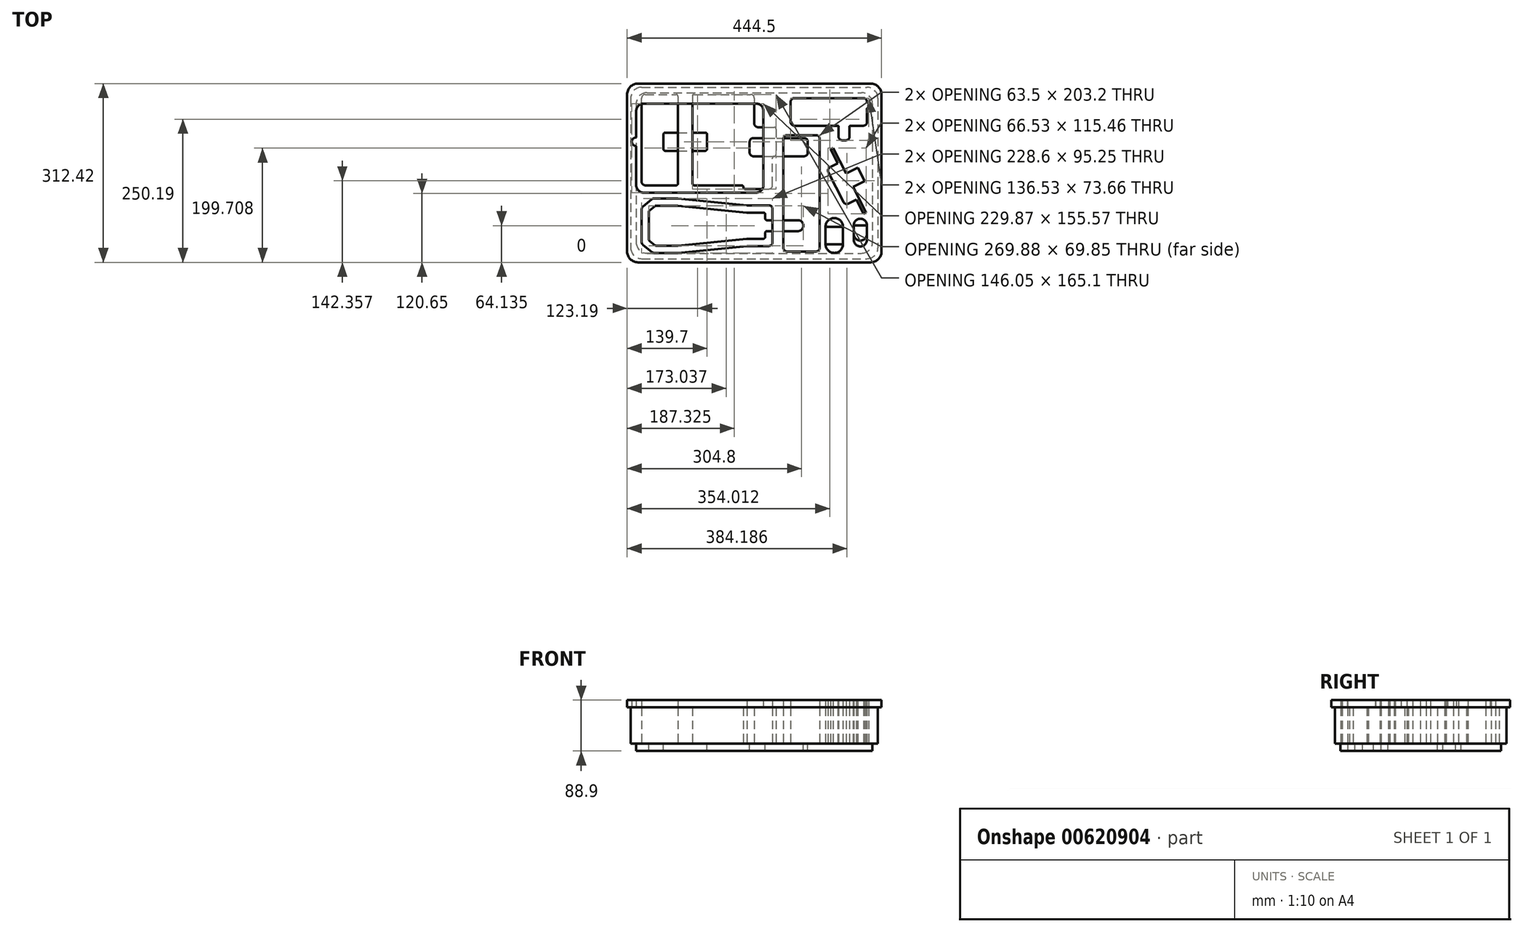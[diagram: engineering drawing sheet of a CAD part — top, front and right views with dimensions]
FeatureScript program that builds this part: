
annotation { "Feature Type Name" : "Feature", "Feature Type Description" : "" }
export const myFeature = defineFeature(function(context is Context, id is Id, definition is map)
    precondition{}
    {
        {
            var Q0;
            Q0=qCreatedBy(makeId("Top.planeOp"),FACE);
            var sketch = newSketch(context, id + "F0", { "sketchPlane" : qUnion([Q0])});
            skLineSegment(sketch, "E0.bottom", {"start": v(-196.85, 149.86) * mm, "end": v(196.85, 149.86) * mm});
            skLineSegment(sketch, "E0.top", {"start": v(-196.85, -149.86) * mm, "end": v(196.85, -149.86) * mm});
            skLineSegment(sketch, "E0.left", {"start": v(-215.9, 130.81) * mm, "end": v(-215.9, -130.81) * mm});
            skLineSegment(sketch, "E0.right", {"start": v(215.9, 130.81) * mm, "end": v(215.9, -130.8) * mm});
            skLineSegment(sketch, "E1.bottom", {"start": v(-196.85, -15.24) * mm, "end": v(-196.85, 130.81) * mm});
            skLineSegment(sketch, "E1.top", {"start": v(31.75, -21.59) * mm, "end": v(31.75, 26.04) * mm});
            skLineSegment(sketch, "E1.right", {"start": v(-190.5, 137.16) * mm, "end": v(-136.52, 137.16) * mm});
            skLineSegment(sketch, "E2.bottom", {"start": v(124.46, -93.98) * mm, "end": v(154.94, -93.98) * mm});
            skLineSegment(sketch, "E2.top", {"start": v(124.46, -124.46) * mm, "end": v(154.94, -124.46) * mm});
            skLineSegment(sketch, "E2.left", {"start": v(124.46, -93.98) * mm, "end": v(124.46, -124.46) * mm});
            skLineSegment(sketch, "E2.right", {"start": v(154.94, -93.98) * mm, "end": v(154.94, -124.46) * mm});
            skLineSegment(sketch, "E3", {"start": v(142.6, -24.8) * mm, "end": v(186.74, -2.32) * mm, "construction": true});
            skLineSegment(sketch, "E4", {"start": v(142.6, -24.8) * mm, "end": v(155.87, -50.83) * mm});
            skLineSegment(sketch, "E5", {"start": v(164.4, -53.6) * mm, "end": v(177.99, -46.7) * mm});
            skLineSegment(sketch, "E6", {"start": v(177.99, -46.7) * mm, "end": v(190.67, -71.59) * mm});
            skLineSegment(sketch, "E7", {"start": v(190.67, -71.59) * mm, "end": v(195.2, -69.28) * mm});
            skLineSegment(sketch, "E8", {"start": v(160.32, -0.82) * mm, "end": v(180.68, 9.56) * mm});
            skLineSegment(sketch, "E9", {"start": v(180.68, 9.56) * mm, "end": v(186.74, -2.32) * mm});
            skPoint(sketch, "E10.visualSharp", {"position": v(158.75, -56.5) * mm});
            skArc(sketch, "E10.filletArc", {"start": v(155.87, -50.83) * mm, "mid": v(159.56, -54) * mm, "end": v(164.4, -53.6) * mm});
            skArc(sketch, "E11.MirrorCS", {"start": v(129.35, 1.22) * mm, "mid": v(128.96, 6.06) * mm, "end": v(132.12, 9.76) * mm});
            skLineSegment(sketch, "E12.MirrorCS", {"start": v(145.7, 16.68) * mm, "end": v(133.02, 41.57) * mm});
            skLineSegment(sketch, "E13.MirrorCS", {"start": v(132.12, 9.76) * mm, "end": v(145.7, 16.68) * mm});
            skPoint(sketch, "E14.MirrorP", {"position": v(126.46, 6.88) * mm});
            skLineSegment(sketch, "E15.MirrorCS", {"start": v(172.42, -24.58) * mm, "end": v(192.8, -14.2) * mm});
            skLineSegment(sketch, "E16.MirrorCS", {"start": v(142.6, -24.8) * mm, "end": v(129.35, 1.22) * mm});
            skLineSegment(sketch, "E17.MirrorCS", {"start": v(192.8, -14.2) * mm, "end": v(186.74, -2.32) * mm});
            skLineSegment(sketch, "E18", {"start": v(172.42, -24.58) * mm, "end": v(195.2, -69.28) * mm});
            skPoint(sketch, "E19.visualSharp", {"position": v(-215.9, 149.86) * mm});
            skArc(sketch, "E19.filletArc", {"start": v(-196.85, 149.86) * mm, "mid": v(-210.32, 144.28) * mm, "end": v(-215.9, 130.81) * mm});
            skPoint(sketch, "E20.visualSharp", {"position": v(215.9, 149.86) * mm});
            skArc(sketch, "E20.filletArc", {"start": v(215.9, 130.81) * mm, "mid": v(210.32, 144.28) * mm, "end": v(196.85, 149.86) * mm});
            skPoint(sketch, "E21.visualSharp", {"position": v(215.9, -149.86) * mm});
            skArc(sketch, "E21.filletArc", {"start": v(196.85, -149.86) * mm, "mid": v(210.32, -144.28) * mm, "end": v(215.9, -130.8) * mm});
            skPoint(sketch, "E22.visualSharp", {"position": v(-215.9, -149.86) * mm});
            skArc(sketch, "E22.filletArc", {"start": v(-215.9, -130.81) * mm, "mid": v(-210.32, -144.28) * mm, "end": v(-196.85, -149.86) * mm});
            skPoint(sketch, "E23.visualSharp", {"position": v(-196.85, -27.94) * mm});
            skPoint(sketch, "E24.visualSharp", {"position": v(31.75, -27.94) * mm});
            skArc(sketch, "E24.filletArc", {"start": v(25.4, -27.94) * mm, "mid": v(29.9, -26.08) * mm, "end": v(31.75, -21.59) * mm});
            skPoint(sketch, "E25.visualSharp", {"position": v(-196.85, 137.16) * mm});
            skArc(sketch, "E25.filletArc", {"start": v(-190.5, 137.16) * mm, "mid": v(-195, 135.3) * mm, "end": v(-196.85, 130.81) * mm});
            skPoint(sketch, "E26.visualSharp", {"position": v(31.75, 137.16) * mm});
            skArc(sketch, "E26.filletArc", {"start": v(31.75, 130.81) * mm, "mid": v(29.9, 135.3) * mm, "end": v(25.4, 137.16) * mm, "construction": true});
            skLineSegment(sketch, "E27.bottom", {"start": v(63.5, 88.9) * mm, "end": v(63.5, 124.46) * mm});
            skLineSegment(sketch, "E27.top", {"start": v(196.85, 88.9) * mm, "end": v(196.85, 112.08) * mm});
            skLineSegment(sketch, "E27.left", {"start": v(69.85, 82.55) * mm, "end": v(146.05, 82.55) * mm});
            skLineSegment(sketch, "E27.right", {"start": v(69.85, 130.81) * mm, "end": v(190.5, 130.81) * mm});
            skLineSegment(sketch, "E28.bottom", {"start": v(147.32, 81.28) * mm, "end": v(147.32, 63.5) * mm});
            skLineSegment(sketch, "E28.top", {"start": v(166.37, 81.28) * mm, "end": v(166.37, 63.5) * mm});
            skLineSegment(sketch, "E28.right", {"start": v(153.67, 57.15) * mm, "end": v(160.02, 57.15) * mm});
            skLineSegment(sketch, "E29.trimOffspring", {"start": v(167.64, 82.55) * mm, "end": v(190.5, 82.55) * mm});
            skLineSegment(sketch, "E30", {"start": v(147.32, 82.55) * mm, "end": v(166.37, 82.55) * mm, "construction": true});
            skPoint(sketch, "E31.visualSharp", {"position": v(63.5, 82.55) * mm});
            skArc(sketch, "E31.filletArc", {"start": v(63.5, 88.9) * mm, "mid": v(65.36, 84.4) * mm, "end": v(69.85, 82.55) * mm});
            skPoint(sketch, "E32.visualSharp", {"position": v(196.85, 82.55) * mm});
            skArc(sketch, "E32.filletArc", {"start": v(190.5, 82.55) * mm, "mid": v(195, 84.4) * mm, "end": v(196.85, 88.9) * mm});
            skArc(sketch, "E33.filletArc", {"start": v(196.85, 124.46) * mm, "mid": v(195, 128.95) * mm, "end": v(190.5, 130.81) * mm});
            skPoint(sketch, "E34.visualSharp", {"position": v(63.5, 130.81) * mm});
            skArc(sketch, "E34.filletArc", {"start": v(69.85, 130.81) * mm, "mid": v(65.36, 128.95) * mm, "end": v(63.5, 124.46) * mm});
            skPoint(sketch, "E35.visualSharp", {"position": v(147.32, 57.15) * mm});
            skArc(sketch, "E35.filletArc", {"start": v(147.32, 63.5) * mm, "mid": v(149.18, 59) * mm, "end": v(153.67, 57.15) * mm});
            skPoint(sketch, "E36.visualSharp", {"position": v(166.37, 57.15) * mm});
            skArc(sketch, "E36.filletArc", {"start": v(160.02, 57.15) * mm, "mid": v(164.51, 59) * mm, "end": v(166.37, 63.5) * mm});
            skLineSegment(sketch, "E37.bottom", {"start": v(173.74, -91.44) * mm, "end": v(196.85, -91.44) * mm});
            skLineSegment(sketch, "E37.left", {"start": v(173.74, -91.44) * mm, "end": v(173.74, -106.68) * mm});
            skLineSegment(sketch, "E37.right", {"start": v(196.85, -91.44) * mm, "end": v(196.85, -106.68) * mm});
            skArc(sketch, "E38", {"start": v(173.74, -106.68) * mm, "mid": v(185.3, -118.24) * mm, "end": v(196.85, -106.68) * mm});
            skLineSegment(sketch, "E39.bottom", {"start": v(-196.85, -139.7) * mm, "end": v(-196.85, -44.45) * mm, "construction": true});
            skLineSegment(sketch, "E39.top", {"start": v(31.75, -139.7) * mm, "end": v(31.75, -44.45) * mm, "construction": true});
            skLineSegment(sketch, "E39.left", {"start": v(-196.85, -139.7) * mm, "end": v(31.75, -139.7) * mm, "construction": true});
            skLineSegment(sketch, "E39.right", {"start": v(-196.85, -44.45) * mm, "end": v(31.75, -44.45) * mm, "construction": true});
            skLineSegment(sketch, "E40", {"start": v(-196.85, -92.08) * mm, "end": v(31.75, -92.07) * mm, "construction": true});
            skLineSegment(sketch, "E41", {"start": v(-196.85, -123.83) * mm, "end": v(31.75, -123.82) * mm, "construction": true});
            skLineSegment(sketch, "E42.MirrorCS", {"start": v(-196.85, -60.33) * mm, "end": v(31.75, -60.32) * mm, "construction": true});
            skLineSegment(sketch, "E43", {"start": v(-196.85, -127.64) * mm, "end": v(31.75, -127.63) * mm, "construction": true});
            skLineSegment(sketch, "E44.MirrorCS", {"start": v(-196.85, -56.51) * mm, "end": v(31.75, -56.51) * mm, "construction": true});
            skLineSegment(sketch, "E45", {"start": v(-177.16, -139.7) * mm, "end": v(-177.16, -44.45) * mm, "construction": true});
            skLineSegment(sketch, "E46", {"start": v(-133.35, -139.7) * mm, "end": v(-133.35, -44.45) * mm, "construction": true});
            skLineSegment(sketch, "E47", {"start": v(-12.7, -139.7) * mm, "end": v(-12.7, -44.45) * mm, "construction": true});
            skLineSegment(sketch, "E48", {"start": v(-196.85, -120.79) * mm, "end": v(-196.85, -63.36) * mm});
            skLineSegment(sketch, "E49", {"start": v(-194.49, -58.42) * mm, "end": v(-178.9, -45.86) * mm});
            skLineSegment(sketch, "E50", {"start": v(-174.92, -44.45) * mm, "end": v(-133.35, -44.45) * mm});
            skLineSegment(sketch, "E51", {"start": v(-133.35, -44.45) * mm, "end": v(-12.7, -56.51) * mm});
            skLineSegment(sketch, "E52", {"start": v(-12.7, -56.51) * mm, "end": v(25.4, -56.51) * mm});
            skLineSegment(sketch, "E53", {"start": v(31.75, -62.86) * mm, "end": v(31.75, -121.28) * mm});
            skLineSegment(sketch, "E54", {"start": v(25.4, -127.63) * mm, "end": v(-12.7, -127.63) * mm});
            skLineSegment(sketch, "E55", {"start": v(-12.7, -127.64) * mm, "end": v(-133.35, -139.7) * mm});
            skLineSegment(sketch, "E56", {"start": v(-133.35, -139.7) * mm, "end": v(-174.92, -139.7) * mm});
            skLineSegment(sketch, "E57", {"start": v(-178.9, -138.3) * mm, "end": v(-194.49, -125.73) * mm});
            skPoint(sketch, "E58.visualSharp", {"position": v(31.75, -127.64) * mm});
            skArc(sketch, "E58.filletArc", {"start": v(25.4, -127.63) * mm, "mid": v(29.9, -125.78) * mm, "end": v(31.75, -121.28) * mm});
            skPoint(sketch, "E59.visualSharp", {"position": v(31.75, -56.51) * mm});
            skArc(sketch, "E59.filletArc", {"start": v(31.75, -62.86) * mm, "mid": v(29.9, -58.37) * mm, "end": v(25.4, -56.51) * mm});
            skPoint(sketch, "E60.visualSharp", {"position": v(-196.85, -123.83) * mm});
            skArc(sketch, "E60.filletArc", {"start": v(-196.85, -120.79) * mm, "mid": v(-196.23, -123.53) * mm, "end": v(-194.49, -125.73) * mm});
            skPoint(sketch, "E61.visualSharp", {"position": v(-177.16, -139.7) * mm});
            skArc(sketch, "E61.filletArc", {"start": v(-178.9, -138.3) * mm, "mid": v(-177.04, -139.34) * mm, "end": v(-174.92, -139.7) * mm});
            skPoint(sketch, "E62.visualSharp", {"position": v(-196.85, -60.33) * mm});
            skArc(sketch, "E62.filletArc", {"start": v(-194.49, -58.42) * mm, "mid": v(-196.23, -60.62) * mm, "end": v(-196.85, -63.36) * mm});
            skPoint(sketch, "E63.visualSharp", {"position": v(-177.16, -44.45) * mm});
            skArc(sketch, "E63.filletArc", {"start": v(-174.92, -44.45) * mm, "mid": v(-177.04, -44.81) * mm, "end": v(-178.9, -45.86) * mm});
            skLineSegment(sketch, "E64", {"start": v(173.74, -106.68) * mm, "end": v(196.85, -106.68) * mm, "construction": true});
            skLineSegment(sketch, "E65.MirrorCS", {"start": v(160.32, -0.82) * mm, "end": v(137.54, 43.88) * mm});
            skLineSegment(sketch, "E66.MirrorCS", {"start": v(133.02, 41.57) * mm, "end": v(137.54, 43.88) * mm});
            skLineSegment(sketch, "E67", {"start": v(198.12, 122.87) * mm, "end": v(198.76, 122.87) * mm});
            skLineSegment(sketch, "E68", {"start": v(200.02, 121.6) * mm, "end": v(200.02, 114.62) * mm});
            skLineSegment(sketch, "E69", {"start": v(198.76, 113.35) * mm, "end": v(198.12, 113.35) * mm});
            skPoint(sketch, "E70.visualSharp", {"position": v(166.37, 82.55) * mm});
            skArc(sketch, "E70.filletArc", {"start": v(167.64, 82.55) * mm, "mid": v(166.74, 82.18) * mm, "end": v(166.37, 81.28) * mm});
            skPoint(sketch, "E71.visualSharp", {"position": v(147.32, 82.55) * mm});
            skArc(sketch, "E71.filletArc", {"start": v(147.32, 81.28) * mm, "mid": v(146.95, 82.18) * mm, "end": v(146.05, 82.55) * mm});
            skPoint(sketch, "E72.visualSharp", {"position": v(200.03, 113.35) * mm});
            skArc(sketch, "E72.filletArc", {"start": v(198.76, 113.35) * mm, "mid": v(199.65, 113.72) * mm, "end": v(200.03, 114.62) * mm});
            skPoint(sketch, "E73.visualSharp", {"position": v(200.03, 122.87) * mm});
            skArc(sketch, "E73.filletArc", {"start": v(200.02, 121.6) * mm, "mid": v(199.65, 122.5) * mm, "end": v(198.76, 122.87) * mm});
            skPoint(sketch, "E74.visualSharp", {"position": v(196.85, 122.87) * mm});
            skArc(sketch, "E74.filletArc", {"start": v(196.85, 124.13) * mm, "mid": v(197.23, 123.24) * mm, "end": v(198.12, 122.87) * mm});
            skPoint(sketch, "E75.visualSharp", {"position": v(196.85, 113.35) * mm});
            skArc(sketch, "E75.filletArc", {"start": v(198.12, 113.35) * mm, "mid": v(197.22, 112.98) * mm, "end": v(196.85, 112.08) * mm});
            skLineSegment(sketch, "E76", {"start": v(-196.85, 54.61) * mm, "end": v(31.75, 54.61) * mm, "construction": true});
            skLineSegment(sketch, "E77", {"start": v(-82.55, -27.94) * mm, "end": v(-82.55, 137.16) * mm, "construction": true});
            skLineSegment(sketch, "E78", {"start": v(0, 149.86) * mm, "end": v(0, -149.86) * mm, "construction": true});
            skLineSegment(sketch, "E79", {"start": v(-215.9, 0) * mm, "end": v(215.9, 0) * mm, "construction": true});
            skPoint(sketch, "E80", {"position": v(0, 0) * mm});
            skPoint(sketch, "E81", {"position": v(-82.55, 54.61) * mm});
            skPoint(sketch, "E82", {"position": v(-133.35, -92.08) * mm});
            skLineSegment(sketch, "E83", {"start": v(63.5, 106.68) * mm, "end": v(196.85, 106.68) * mm, "construction": true});
            skLineSegment(sketch, "E84", {"start": v(130.18, 130.81) * mm, "end": v(130.18, 82.55) * mm, "construction": true});
            skPoint(sketch, "E85", {"position": v(130.18, 106.68) * mm});
            skLineSegment(sketch, "E86", {"start": v(172.42, -24.58) * mm, "end": v(160.32, -0.82) * mm, "construction": true});
            skPoint(sketch, "E87", {"position": v(166.37, -12.7) * mm});
            skLineSegment(sketch, "E88", {"start": v(196.85, 124.46) * mm, "end": v(196.85, 124.13) * mm});
            skLineSegment(sketch, "E89", {"start": v(196.85, 124.13) * mm, "end": v(196.85, 112.08) * mm, "construction": true});
            skArc(sketch, "E90", {"start": v(31.75, -21.59) * mm, "mid": v(29.9, -26.08) * mm, "end": v(25.4, -27.94) * mm});
            skLineSegment(sketch, "E91.bottom", {"start": v(107.95, -137.16) * mm, "end": v(57.15, -137.16) * mm});
            skLineSegment(sketch, "E91.top", {"start": v(107.95, 66.04) * mm, "end": v(57.15, 66.04) * mm});
            skLineSegment(sketch, "E91.left", {"start": v(114.3, -130.8) * mm, "end": v(114.3, 59.7) * mm});
            skLineSegment(sketch, "E91.right", {"start": v(50.8, -130.8) * mm, "end": v(50.8, 59.7) * mm});
            skLineSegment(sketch, "E92", {"start": v(82.55, -137.16) * mm, "end": v(82.55, 66.04) * mm, "construction": true});
            skLineSegment(sketch, "E93", {"start": v(114.3, -35.56) * mm, "end": v(50.8, -35.56) * mm, "construction": true});
            skPoint(sketch, "E94", {"position": v(82.55, -35.56) * mm});
            skPoint(sketch, "E95.visualSharp", {"position": v(114.3, -137.16) * mm});
            skArc(sketch, "E95.filletArc", {"start": v(107.95, -137.16) * mm, "mid": v(112.44, -135.3) * mm, "end": v(114.3, -130.8) * mm});
            skPoint(sketch, "E96.visualSharp", {"position": v(50.8, -137.16) * mm});
            skArc(sketch, "E96.filletArc", {"start": v(50.8, -130.8) * mm, "mid": v(52.66, -135.3) * mm, "end": v(57.15, -137.16) * mm});
            skPoint(sketch, "E97.visualSharp", {"position": v(50.8, 66.04) * mm});
            skArc(sketch, "E97.filletArc", {"start": v(57.15, 66.04) * mm, "mid": v(52.66, 64.18) * mm, "end": v(50.8, 59.7) * mm});
            skPoint(sketch, "E98.visualSharp", {"position": v(114.3, 66.04) * mm});
            skArc(sketch, "E98.filletArc", {"start": v(114.3, 59.7) * mm, "mid": v(112.44, 64.18) * mm, "end": v(107.95, 66.04) * mm});
            skLineSegment(sketch, "E99.left", {"start": v(-107.95, 133.99) * mm, "end": v(-107.95, -18.41) * mm});
            skLineSegment(sketch, "E99.right", {"start": v(-133.35, 133.99) * mm, "end": v(-133.35, -18.41) * mm});
            skLineSegment(sketch, "E100", {"start": v(34.93, 80.01) * mm, "end": v(34.92, 80.01) * mm});
            skLineSegment(sketch, "E101.MirrorCS", {"start": v(34.93, 29.21) * mm, "end": v(34.93, 29.21) * mm});
            skLineSegment(sketch, "E102", {"start": v(38.1, 76.84) * mm, "end": v(38.1, 32.39) * mm});
            skLineSegment(sketch, "E103", {"start": v(-104.77, 137.16) * mm, "end": v(-6.35, 137.16) * mm});
            skLineSegment(sketch, "E104", {"start": v(31.75, 83.19) * mm, "end": v(31.75, 130.81) * mm, "construction": true});
            skLineSegment(sketch, "E105", {"start": v(31.75, 29.21) * mm, "end": v(31.75, 80.01) * mm, "construction": true});
            skLineSegment(sketch, "E106", {"start": v(-133.35, 137.16) * mm, "end": v(-107.95, 137.16) * mm, "construction": true});
            skPoint(sketch, "E107.visualSharp", {"position": v(-107.95, 137.16) * mm});
            skArc(sketch, "E107.filletArc", {"start": v(-104.77, 137.16) * mm, "mid": v(-107.02, 136.23) * mm, "end": v(-107.95, 133.99) * mm});
            skPoint(sketch, "E108.visualSharp", {"position": v(-133.35, 137.16) * mm});
            skArc(sketch, "E108.filletArc", {"start": v(-133.35, 133.99) * mm, "mid": v(-134.28, 136.23) * mm, "end": v(-136.52, 137.16) * mm});
            skPoint(sketch, "E109.visualSharp", {"position": v(31.75, 80.01) * mm});
            skPoint(sketch, "E110.visualSharp", {"position": v(31.75, 29.21) * mm});
            skArc(sketch, "E110.filletArc", {"start": v(34.93, 29.21) * mm, "mid": v(32.68, 28.28) * mm, "end": v(31.75, 26.04) * mm});
            skPoint(sketch, "E111.visualSharp", {"position": v(38.1, 29.21) * mm});
            skArc(sketch, "E111.filletArc", {"start": v(34.93, 29.21) * mm, "mid": v(37.17, 30.14) * mm, "end": v(38.1, 32.39) * mm});
            skPoint(sketch, "E112.visualSharp", {"position": v(38.1, 80.01) * mm});
            skArc(sketch, "E112.filletArc", {"start": v(38.1, 76.84) * mm, "mid": v(37.17, 79.08) * mm, "end": v(34.92, 80.01) * mm});
            skLineSegment(sketch, "E113", {"start": v(0, 130.81) * mm, "end": v(0, 86.36) * mm});
            skLineSegment(sketch, "E114", {"start": v(6.35, 80.01) * mm, "end": v(34.93, 80.01) * mm});
            skPoint(sketch, "E115.visualSharp", {"position": v(0, 80.01) * mm});
            skArc(sketch, "E115.filletArc", {"start": v(0, 86.36) * mm, "mid": v(1.86, 81.87) * mm, "end": v(6.35, 80.01) * mm});
            skLineSegment(sketch, "E116", {"start": v(-6.35, 137.16) * mm, "end": v(0, 137.16) * mm, "construction": true});
            skLineSegment(sketch, "E117", {"start": v(0, 137.16) * mm, "end": v(25.4, 137.16) * mm, "construction": true});
            skPoint(sketch, "E118.visualSharp", {"position": v(0, 137.16) * mm});
            skArc(sketch, "E118.filletArc", {"start": v(0, 130.81) * mm, "mid": v(-1.86, 135.3) * mm, "end": v(-6.35, 137.16) * mm});
            skLineSegment(sketch, "E119", {"start": v(-6.35, 137.16) * mm, "end": v(-6.35, 137.16) * mm});
            skLineSegment(sketch, "E120", {"start": v(-19.05, -24.76) * mm, "end": v(-19.05, -24.76) * mm});
            skLineSegment(sketch, "E121", {"start": v(-22.22, -21.59) * mm, "end": v(-104.78, -21.59) * mm});
            skLineSegment(sketch, "E122", {"start": v(-133.35, -21.59) * mm, "end": v(-133.35, -24.76) * mm, "construction": true});
            skLineSegment(sketch, "E123", {"start": v(-15.88, -27.94) * mm, "end": v(25.4, -27.94) * mm});
            skLineSegment(sketch, "E124", {"start": v(-107.95, -21.59) * mm, "end": v(-107.95, -24.76) * mm, "construction": true});
            skPoint(sketch, "E125.visualSharp", {"position": v(-196.85, -21.59) * mm});
            skArc(sketch, "E125.filletArc", {"start": v(-196.85, -15.24) * mm, "mid": v(-195, -19.73) * mm, "end": v(-190.5, -21.59) * mm});
            skPoint(sketch, "E126.visualSharp", {"position": v(-19.05, -21.59) * mm});
            skArc(sketch, "E126.filletArc", {"start": v(-19.05, -24.76) * mm, "mid": v(-19.98, -22.52) * mm, "end": v(-22.22, -21.59) * mm});
            skPoint(sketch, "E127.visualSharp", {"position": v(-19.05, -27.94) * mm});
            skArc(sketch, "E127.filletArc", {"start": v(-19.05, -24.76) * mm, "mid": v(-18.12, -27.01) * mm, "end": v(-15.88, -27.94) * mm});
            skLineSegment(sketch, "E128", {"start": v(-136.53, -21.59) * mm, "end": v(-190.5, -21.59) * mm});
            skPoint(sketch, "E129.visualSharp", {"position": v(-133.35, -21.59) * mm});
            skArc(sketch, "E129.filletArc", {"start": v(-136.53, -21.59) * mm, "mid": v(-134.28, -20.66) * mm, "end": v(-133.35, -18.41) * mm});
            skPoint(sketch, "E130.visualSharp", {"position": v(-107.95, -21.59) * mm});
            skArc(sketch, "E130.filletArc", {"start": v(-107.95, -18.41) * mm, "mid": v(-107.02, -20.66) * mm, "end": v(-104.78, -21.59) * mm});
            skSolve(sketch);
        }
        {
            var Q0;
            Q0=qSketchRegion(id+"F0",true);
            extrude(context, id + "F1", {"entities" : qUnion([Q0]), "depth" : 63.5 * mm, "offsetDistance" : 25.4 * mm});
        }
        {
            var Q0;
            Q0=qCreatedBy(makeId("Top.planeOp"),FACE);
            var sketch = newSketch(context, id + "F2", { "sketchPlane" : qUnion([Q0])});
            skLineSegment(sketch, "E131.0", {"start": v(-215.9, 149.86) * mm, "end": v(215.9, 149.86) * mm, "construction": true});
            skLineSegment(sketch, "E132.0", {"start": v(-215.9, 149.86) * mm, "end": v(-215.9, -149.86) * mm, "construction": true});
            skLineSegment(sketch, "E133.0", {"start": v(215.9, 149.86) * mm, "end": v(215.9, -149.86) * mm, "construction": true});
            skLineSegment(sketch, "E134.0", {"start": v(-190.26, -149.86) * mm, "end": v(215.9, -149.86) * mm, "construction": true});
            skPoint(sketch, "E135.orphan", {"position": v(-196.85, 149.86) * mm});
            skPoint(sketch, "E136.orphan", {"position": v(-215.9, 130.81) * mm});
            skPoint(sketch, "E137.orphan", {"position": v(196.85, 149.86) * mm});
            skPoint(sketch, "E138.orphan", {"position": v(215.9, 130.81) * mm});
            skPoint(sketch, "E139.orphan", {"position": v(215.9, -130.8) * mm});
            skPoint(sketch, "E140.orphan", {"position": v(196.85, -149.86) * mm});
            skPoint(sketch, "E141.orphan", {"position": v(-196.85, -149.86) * mm});
            skPoint(sketch, "E142.orphan", {"position": v(-215.9, -130.81) * mm});
            skPoint(sketch, "E143", {"position": v(0, 0) * mm});
            skLineSegment(sketch, "E144", {"start": v(0, 149.86) * mm, "end": v(0, -149.86) * mm, "construction": true});
            skPoint(sketch, "E144.startSnap0", {"position": v(0, 149.86) * mm});
            skLineSegment(sketch, "E145", {"start": v(-215.9, 0) * mm, "end": v(215.9, 0) * mm, "construction": true});
            skLineSegment(sketch, "E146.bottom", {"start": v(-187.32, 140.34) * mm, "end": v(187.33, 140.34) * mm});
            skLineSegment(sketch, "E146.top", {"start": v(-187.33, -140.33) * mm, "end": v(187.32, -140.33) * mm});
            skLineSegment(sketch, "E146.left", {"start": v(-206.38, 121.29) * mm, "end": v(-206.38, -121.28) * mm});
            skLineSegment(sketch, "E146.right", {"start": v(206.38, 121.29) * mm, "end": v(206.38, -121.28) * mm});
            skPoint(sketch, "E147.visualSharp", {"position": v(-206.38, 140.34) * mm});
            skPoint(sketch, "E148.visualSharp", {"position": v(206.38, 140.34) * mm});
            skPoint(sketch, "E149.visualSharp", {"position": v(206.38, -140.33) * mm});
            skPoint(sketch, "E150.visualSharp", {"position": v(-206.38, -140.33) * mm});
            skLineSegment(sketch, "E151.0.0", {"start": v(-12.7, -127.63) * mm, "end": v(25.4, -127.63) * mm, "construction": true});
            skArc(sketch, "E151.0.1", {"start": v(25.4, -127.63) * mm, "mid": v(29.9, -125.78) * mm, "end": v(31.75, -121.28) * mm, "construction": true});
            skLineSegment(sketch, "E151.0.2", {"start": v(31.75, -121.28) * mm, "end": v(31.75, -62.86) * mm, "construction": true});
            skArc(sketch, "E151.0.3", {"start": v(31.75, -62.86) * mm, "mid": v(29.9, -58.37) * mm, "end": v(25.4, -56.51) * mm, "construction": true});
            skLineSegment(sketch, "E151.0.4", {"start": v(25.4, -56.51) * mm, "end": v(-12.7, -56.51) * mm, "construction": true});
            skLineSegment(sketch, "E151.0.5", {"start": v(-12.7, -56.52) * mm, "end": v(-133.35, -44.45) * mm, "construction": true});
            skLineSegment(sketch, "E151.0.6", {"start": v(-133.35, -44.45) * mm, "end": v(-174.92, -44.45) * mm, "construction": true});
            skArc(sketch, "E151.0.7", {"start": v(-174.92, -44.45) * mm, "mid": v(-177.04, -44.81) * mm, "end": v(-178.9, -45.86) * mm, "construction": true});
            skLineSegment(sketch, "E151.0.8", {"start": v(-178.9, -45.86) * mm, "end": v(-194.49, -58.42) * mm, "construction": true});
            skArc(sketch, "E151.0.9", {"start": v(-194.49, -58.42) * mm, "mid": v(-196.23, -60.62) * mm, "end": v(-196.85, -63.36) * mm, "construction": true});
            skLineSegment(sketch, "E151.0.10", {"start": v(-196.85, -63.36) * mm, "end": v(-196.85, -120.79) * mm, "construction": true});
            skArc(sketch, "E151.0.11", {"start": v(-196.85, -120.79) * mm, "mid": v(-196.23, -123.53) * mm, "end": v(-194.49, -125.73) * mm, "construction": true});
            skLineSegment(sketch, "E151.0.12", {"start": v(-194.49, -125.73) * mm, "end": v(-178.9, -138.3) * mm, "construction": true});
            skArc(sketch, "E151.0.13", {"start": v(-178.9, -138.3) * mm, "mid": v(-177.04, -139.34) * mm, "end": v(-174.92, -139.7) * mm, "construction": true});
            skLineSegment(sketch, "E151.0.14", {"start": v(-174.92, -139.7) * mm, "end": v(-133.35, -139.7) * mm, "construction": true});
            skLineSegment(sketch, "E151.0.15", {"start": v(-133.35, -139.7) * mm, "end": v(-12.7, -127.64) * mm, "construction": true});
            skArc(sketch, "E152.filletArc", {"start": v(-187.32, 140.34) * mm, "mid": v(-200.8, 134.76) * mm, "end": v(-206.38, 121.29) * mm});
            skArc(sketch, "E153.filletArc", {"start": v(206.38, 121.29) * mm, "mid": v(200.8, 134.76) * mm, "end": v(187.33, 140.34) * mm});
            skArc(sketch, "E154.filletArc", {"start": v(187.32, -140.33) * mm, "mid": v(200.8, -134.76) * mm, "end": v(206.37, -121.28) * mm});
            skArc(sketch, "E155.filletArc", {"start": v(-206.38, -121.28) * mm, "mid": v(-200.8, -134.76) * mm, "end": v(-187.33, -140.33) * mm});
            skLineSegment(sketch, "E156.0", {"start": v(-173.55, -57.85) * mm, "end": v(-182.97, -65.45) * mm});
            skLineSegment(sketch, "E156.1", {"start": v(-134.14, -57.15) * mm, "end": v(-171.56, -57.15) * mm});
            skLineSegment(sketch, "E156.2", {"start": v(-184.15, -67.92) * mm, "end": v(-184.15, -116.23) * mm});
            skLineSegment(sketch, "E156.3", {"start": v(-13.5, -69.2) * mm, "end": v(-133.83, -57.17) * mm});
            skLineSegment(sketch, "E156.4", {"start": v(15.88, -69.21) * mm, "end": v(-13.18, -69.21) * mm});
            skLineSegment(sketch, "E156.5", {"start": v(19.05, -111.76) * mm, "end": v(19.05, -104.78) * mm});
            skLineSegment(sketch, "E156.6", {"start": v(-182.97, -118.7) * mm, "end": v(-173.55, -126.3) * mm});
            skLineSegment(sketch, "E156.7", {"start": v(-171.56, -127) * mm, "end": v(-134.14, -127) * mm});
            skLineSegment(sketch, "E156.8", {"start": v(-133.83, -126.98) * mm, "end": v(-13.5, -114.95) * mm});
            skLineSegment(sketch, "E156.9", {"start": v(-13.18, -114.93) * mm, "end": v(15.88, -114.93) * mm});
            skLineSegment(sketch, "E157", {"start": v(22.23, -82.55) * mm, "end": v(76.2, -82.55) * mm});
            skLineSegment(sketch, "E158", {"start": v(-184.15, -92.08) * mm, "end": v(76.2, -92.08) * mm, "construction": true});
            skLineSegment(sketch, "E159", {"start": v(76.2, -82.55) * mm, "end": v(76.2, -92.08) * mm, "construction": true});
            skLineSegment(sketch, "E160.MirrorCS", {"start": v(22.23, -101.6) * mm, "end": v(76.2, -101.6) * mm});
            skLineSegment(sketch, "E161.MirrorCS", {"start": v(76.2, -101.6) * mm, "end": v(76.2, -92.08) * mm, "construction": true});
            skLineSegment(sketch, "E162", {"start": v(19.05, -79.37) * mm, "end": v(19.05, -72.39) * mm});
            skPoint(sketch, "E163.orphan", {"position": v(19.05, -92.08) * mm});
            skArc(sketch, "E164", {"start": v(76.2, -82.55) * mm, "mid": v(85.73, -92.08) * mm, "end": v(76.2, -101.6) * mm});
            skLineSegment(sketch, "E165.bottom", {"start": v(-1.78, 60.96) * mm, "end": v(87.12, 60.96) * mm});
            skLineSegment(sketch, "E165.top", {"start": v(-1.78, 29.21) * mm, "end": v(87.12, 29.21) * mm});
            skLineSegment(sketch, "E165.left", {"start": v(-8.13, 54.61) * mm, "end": v(-8.13, 35.56) * mm});
            skLineSegment(sketch, "E165.right", {"start": v(93.47, 54.61) * mm, "end": v(93.47, 35.56) * mm});
            skPoint(sketch, "E166.visualSharp", {"position": v(-8.13, 60.96) * mm});
            skArc(sketch, "E166.filletArc", {"start": v(-1.78, 60.96) * mm, "mid": v(-6.27, 59.1) * mm, "end": v(-8.13, 54.61) * mm});
            skPoint(sketch, "E167.visualSharp", {"position": v(93.47, 60.96) * mm});
            skArc(sketch, "E167.filletArc", {"start": v(93.47, 54.61) * mm, "mid": v(91.61, 59.1) * mm, "end": v(87.12, 60.96) * mm});
            skPoint(sketch, "E168.visualSharp", {"position": v(93.47, 29.21) * mm});
            skArc(sketch, "E168.filletArc", {"start": v(87.12, 29.21) * mm, "mid": v(91.61, 31.07) * mm, "end": v(93.47, 35.56) * mm});
            skPoint(sketch, "E169.visualSharp", {"position": v(-8.13, 29.21) * mm});
            skArc(sketch, "E169.filletArc", {"start": v(-8.13, 35.56) * mm, "mid": v(-6.27, 31.07) * mm, "end": v(-1.78, 29.21) * mm});
            skPoint(sketch, "E170.visualSharp", {"position": v(19.05, -69.21) * mm});
            skArc(sketch, "E170.filletArc", {"start": v(19.05, -72.39) * mm, "mid": v(18.12, -70.14) * mm, "end": v(15.88, -69.21) * mm});
            skPoint(sketch, "E171.visualSharp", {"position": v(19.05, -82.55) * mm});
            skArc(sketch, "E171.filletArc", {"start": v(19.05, -79.37) * mm, "mid": v(19.98, -81.62) * mm, "end": v(22.23, -82.55) * mm});
            skPoint(sketch, "E172.visualSharp", {"position": v(19.05, -101.6) * mm});
            skArc(sketch, "E172.filletArc", {"start": v(22.23, -101.6) * mm, "mid": v(19.98, -102.53) * mm, "end": v(19.05, -104.78) * mm});
            skPoint(sketch, "E173.visualSharp", {"position": v(19.05, -114.94) * mm});
            skArc(sketch, "E173.filletArc", {"start": v(15.88, -114.94) * mm, "mid": v(18.12, -114) * mm, "end": v(19.05, -111.76) * mm});
            skPoint(sketch, "E174.visualSharp", {"position": v(-184.15, -66.4) * mm});
            skArc(sketch, "E174.filletArc", {"start": v(-182.97, -65.45) * mm, "mid": v(-183.84, -66.55) * mm, "end": v(-184.15, -67.92) * mm});
            skPoint(sketch, "E175.visualSharp", {"position": v(-172.68, -57.15) * mm});
            skArc(sketch, "E175.filletArc", {"start": v(-171.56, -57.15) * mm, "mid": v(-172.62, -57.33) * mm, "end": v(-173.55, -57.85) * mm});
            skPoint(sketch, "E176.visualSharp", {"position": v(-133.98, -57.15) * mm});
            skArc(sketch, "E176.filletArc", {"start": v(-133.83, -57.17) * mm, "mid": v(-133.98, -57.15) * mm, "end": v(-134.14, -57.15) * mm});
            skPoint(sketch, "E177.visualSharp", {"position": v(-184.15, -117.75) * mm});
            skArc(sketch, "E177.filletArc", {"start": v(-184.15, -116.23) * mm, "mid": v(-183.84, -117.6) * mm, "end": v(-182.97, -118.7) * mm});
            skPoint(sketch, "E178.visualSharp", {"position": v(-172.68, -127) * mm});
            skArc(sketch, "E178.filletArc", {"start": v(-173.55, -126.3) * mm, "mid": v(-172.62, -126.82) * mm, "end": v(-171.56, -127) * mm});
            skPoint(sketch, "E179.visualSharp", {"position": v(-133.98, -127) * mm});
            skArc(sketch, "E179.filletArc", {"start": v(-134.14, -127) * mm, "mid": v(-133.98, -127) * mm, "end": v(-133.83, -126.98) * mm});
            skPoint(sketch, "E180.visualSharp", {"position": v(-13.33, -114.93) * mm});
            skArc(sketch, "E180.filletArc", {"start": v(-13.18, -114.93) * mm, "mid": v(-13.33, -114.94) * mm, "end": v(-13.5, -114.95) * mm});
            skPoint(sketch, "E181.visualSharp", {"position": v(-13.33, -69.21) * mm});
            skArc(sketch, "E181.filletArc", {"start": v(-13.5, -69.2) * mm, "mid": v(-13.33, -69.21) * mm, "end": v(-13.18, -69.21) * mm});
            skLineSegment(sketch, "E182.0", {"start": v(-196.85, 54.61) * mm, "end": v(31.75, 54.61) * mm, "construction": true});
            skLineSegment(sketch, "E183.0", {"start": v(-133.35, 133.99) * mm, "end": v(-133.35, -18.41) * mm, "construction": true});
            skLineSegment(sketch, "E184.0", {"start": v(-107.95, 133.99) * mm, "end": v(-107.95, -18.41) * mm, "construction": true});
            skLineSegment(sketch, "E185", {"start": v(-158.75, 54.61) * mm, "end": v(-158.75, 67.31) * mm});
            skLineSegment(sketch, "E186", {"start": v(-155.57, 70.49) * mm, "end": v(-85.72, 70.49) * mm});
            skLineSegment(sketch, "E187", {"start": v(-82.55, 67.31) * mm, "end": v(-82.55, 54.61) * mm});
            skLineSegment(sketch, "E188.MirrorCS", {"start": v(-82.55, 41.91) * mm, "end": v(-82.55, 54.61) * mm});
            skLineSegment(sketch, "E189.MirrorCS", {"start": v(-158.75, 54.61) * mm, "end": v(-158.75, 41.91) * mm});
            skLineSegment(sketch, "E190.MirrorCS", {"start": v(-155.57, 38.74) * mm, "end": v(-85.72, 38.74) * mm});
            skPoint(sketch, "E191.visualSharp", {"position": v(-158.75, 70.49) * mm});
            skArc(sketch, "E191.filletArc", {"start": v(-155.57, 70.49) * mm, "mid": v(-157.82, 69.56) * mm, "end": v(-158.75, 67.31) * mm});
            skPoint(sketch, "E192.visualSharp", {"position": v(-158.75, 38.74) * mm});
            skArc(sketch, "E192.filletArc", {"start": v(-158.75, 41.91) * mm, "mid": v(-157.82, 39.66) * mm, "end": v(-155.57, 38.74) * mm});
            skPoint(sketch, "E193.visualSharp", {"position": v(-82.55, 38.74) * mm});
            skArc(sketch, "E193.filletArc", {"start": v(-85.72, 38.74) * mm, "mid": v(-83.48, 39.66) * mm, "end": v(-82.55, 41.91) * mm});
            skPoint(sketch, "E194.visualSharp", {"position": v(-82.55, 70.49) * mm});
            skArc(sketch, "E194.filletArc", {"start": v(-82.55, 67.31) * mm, "mid": v(-83.48, 69.56) * mm, "end": v(-85.72, 70.49) * mm});
            skSolve(sketch);
        }
        {
            var Q0;
            Q0=qSketchRegion(id+"F2",true);
            extrude(context, id + "F3", {"entities" : qUnion([Q0]), "oppositeDirection" : true, "depth" : 12.7 * mm, "offsetDistance" : 25.4 * mm});
        }
        {
            var Q0;
            Q0=makeQuery(id+"F1.opExtrude","CAP_FACE",FACE,{"disambiguationData":[OSD([sQuery(id+"F0.wireOp",EDGE,"E0.bottom"),sQuery(id+"F0.wireOp",EDGE,"E0.top"),sQuery(id+"F0.wireOp",EDGE,"E0.left"),sQuery(id+"F0.wireOp",EDGE,"E0.right"),sQuery(id+"F0.wireOp",EDGE,"E1.bottom"),sQuery(id+"F0.wireOp",EDGE,"E1.top"),sQuery(id+"F0.wireOp",EDGE,"E1.left"),sQuery(id+"F0.wireOp",EDGE,"E1.right"),sQuery(id+"F0.wireOp",EDGE,"E2.bottom"),sQuery(id+"F0.wireOp",EDGE,"E2.top"),sQuery(id+"F0.wireOp",EDGE,"E2.left"),sQuery(id+"F0.wireOp",EDGE,"E2.right"),sQuery(id+"F0.wireOp",EDGE,"E4"),sQuery(id+"F0.wireOp",EDGE,"E5"),sQuery(id+"F0.wireOp",EDGE,"E6"),sQuery(id+"F0.wireOp",EDGE,"E7"),sQuery(id+"F0.wireOp",EDGE,"E8"),sQuery(id+"F0.wireOp",EDGE,"E9"),sQuery(id+"F0.wireOp",EDGE,"E10.filletArc"),sQuery(id+"F0.wireOp",EDGE,"E11.MirrorCS"),sQuery(id+"F0.wireOp",EDGE,"E12.MirrorCS"),sQuery(id+"F0.wireOp",EDGE,"E13.MirrorCS"),sQuery(id+"F0.wireOp",EDGE,"E15.MirrorCS"),sQuery(id+"F0.wireOp",EDGE,"E16.MirrorCS"),sQuery(id+"F0.wireOp",EDGE,"E17.MirrorCS"),sQuery(id+"F0.wireOp",EDGE,"E18"),sQuery(id+"F0.wireOp",EDGE,"E19.filletArc"),sQuery(id+"F0.wireOp",EDGE,"E20.filletArc"),sQuery(id+"F0.wireOp",EDGE,"E21.filletArc"),sQuery(id+"F0.wireOp",EDGE,"E22.filletArc"),sQuery(id+"F0.wireOp",EDGE,"E23.filletArc"),sQuery(id+"F0.wireOp",EDGE,"E25.filletArc"),sQuery(id+"F0.wireOp",EDGE,"E26.filletArc"),sQuery(id+"F0.wireOp",EDGE,"E27.bottom"),sQuery(id+"F0.wireOp",EDGE,"E27.top"),sQuery(id+"F0.wireOp",EDGE,"E27.left"),sQuery(id+"F0.wireOp",EDGE,"E27.right"),sQuery(id+"F0.wireOp",EDGE,"E28.bottom"),sQuery(id+"F0.wireOp",EDGE,"E28.top"),sQuery(id+"F0.wireOp",EDGE,"E28.right"),sQuery(id+"F0.wireOp",EDGE,"E29.trimOffspring"),sQuery(id+"F0.wireOp",EDGE,"E31.filletArc"),sQuery(id+"F0.wireOp",EDGE,"E32.filletArc"),sQuery(id+"F0.wireOp",EDGE,"E33.filletArc"),sQuery(id+"F0.wireOp",EDGE,"E34.filletArc"),sQuery(id+"F0.wireOp",EDGE,"E35.filletArc"),sQuery(id+"F0.wireOp",EDGE,"E36.filletArc"),sQuery(id+"F0.wireOp",EDGE,"E37.bottom"),sQuery(id+"F0.wireOp",EDGE,"E37.left"),sQuery(id+"F0.wireOp",EDGE,"E37.right"),sQuery(id+"F0.wireOp",EDGE,"E38"),sQuery(id+"F0.wireOp",EDGE,"E48"),sQuery(id+"F0.wireOp",EDGE,"E49"),sQuery(id+"F0.wireOp",EDGE,"E50"),sQuery(id+"F0.wireOp",EDGE,"E51"),sQuery(id+"F0.wireOp",EDGE,"E52"),sQuery(id+"F0.wireOp",EDGE,"E53"),sQuery(id+"F0.wireOp",EDGE,"E54"),sQuery(id+"F0.wireOp",EDGE,"E55"),sQuery(id+"F0.wireOp",EDGE,"E56"),sQuery(id+"F0.wireOp",EDGE,"E57"),sQuery(id+"F0.wireOp",EDGE,"E58.filletArc"),sQuery(id+"F0.wireOp",EDGE,"E59.filletArc"),sQuery(id+"F0.wireOp",EDGE,"E60.filletArc"),sQuery(id+"F0.wireOp",EDGE,"E61.filletArc"),sQuery(id+"F0.wireOp",EDGE,"E62.filletArc"),sQuery(id+"F0.wireOp",EDGE,"E63.filletArc"),sQuery(id+"F0.wireOp",EDGE,"E65.MirrorCS"),sQuery(id+"F0.wireOp",EDGE,"E66.MirrorCS"),sQuery(id+"F0.wireOp",EDGE,"E67"),sQuery(id+"F0.wireOp",EDGE,"E68"),sQuery(id+"F0.wireOp",EDGE,"E69"),sQuery(id+"F0.wireOp",EDGE,"E70.filletArc"),sQuery(id+"F0.wireOp",EDGE,"E71.filletArc"),sQuery(id+"F0.wireOp",EDGE,"E72.filletArc"),sQuery(id+"F0.wireOp",EDGE,"E73.filletArc"),sQuery(id+"F0.wireOp",EDGE,"E74.filletArc"),sQuery(id+"F0.wireOp",EDGE,"E75.filletArc"),sQuery(id+"F0.wireOp",EDGE,"E88"),sQuery(id+"F0.wireOp",EDGE,"E90"),sQuery(id+"F0.wireOp",EDGE,"E91.bottom"),sQuery(id+"F0.wireOp",EDGE,"E91.top"),sQuery(id+"F0.wireOp",EDGE,"E91.left"),sQuery(id+"F0.wireOp",EDGE,"E91.right"),sQuery(id+"F0.wireOp",EDGE,"E95.filletArc"),sQuery(id+"F0.wireOp",EDGE,"E96.filletArc"),sQuery(id+"F0.wireOp",EDGE,"E97.filletArc"),sQuery(id+"F0.wireOp",EDGE,"E98.filletArc")])],"isStart":false});
            var sketch = newSketch(context, id + "F4", { "sketchPlane" : qUnion([Q0])});
            skLineSegment(sketch, "E195.bottom", {"start": v(-203.2, 156.21) * mm, "end": v(203.2, 156.21) * mm});
            skLineSegment(sketch, "E195.top", {"start": v(-203.2, -156.2) * mm, "end": v(203.2, -156.2) * mm});
            skLineSegment(sketch, "E195.left", {"start": v(-222.25, 137.16) * mm, "end": v(-222.25, -137.16) * mm});
            skLineSegment(sketch, "E195.right", {"start": v(222.25, 137.16) * mm, "end": v(222.25, -137.16) * mm});
            skLineSegment(sketch, "E196.bottom", {"start": v(-196.85, -21.59) * mm, "end": v(-196.85, 130.81) * mm, "construction": true});
            skLineSegment(sketch, "E196.top", {"start": v(31.75, -21.59) * mm, "end": v(31.75, 130.81) * mm, "construction": true});
            skLineSegment(sketch, "E196.left", {"start": v(-190.5, -27.94) * mm, "end": v(25.4, -27.94) * mm, "construction": true});
            skLineSegment(sketch, "E196.right", {"start": v(-190.5, 137.16) * mm, "end": v(25.4, 137.16) * mm, "construction": true});
            skLineSegment(sketch, "E197.bottom", {"start": v(124.46, -93.98) * mm, "end": v(154.94, -93.98) * mm});
            skLineSegment(sketch, "E197.top", {"start": v(124.46, -124.46) * mm, "end": v(154.94, -124.46) * mm});
            skLineSegment(sketch, "E197.left", {"start": v(124.46, -93.98) * mm, "end": v(124.46, -124.46) * mm});
            skLineSegment(sketch, "E197.right", {"start": v(154.94, -93.98) * mm, "end": v(154.94, -124.46) * mm});
            skLineSegment(sketch, "E198", {"start": v(142.6, -24.8) * mm, "end": v(186.74, -2.32) * mm, "construction": true});
            skLineSegment(sketch, "E199", {"start": v(142.6, -24.8) * mm, "end": v(155.87, -50.83) * mm});
            skLineSegment(sketch, "E200", {"start": v(164.4, -53.6) * mm, "end": v(177.99, -46.7) * mm});
            skLineSegment(sketch, "E201", {"start": v(177.99, -46.7) * mm, "end": v(190.67, -71.59) * mm});
            skLineSegment(sketch, "E202", {"start": v(190.67, -71.59) * mm, "end": v(195.2, -69.28) * mm});
            skLineSegment(sketch, "E203", {"start": v(160.32, -0.82) * mm, "end": v(180.68, 9.56) * mm});
            skLineSegment(sketch, "E204", {"start": v(180.68, 9.56) * mm, "end": v(186.74, -2.32) * mm});
            skPoint(sketch, "E205.visualSharp", {"position": v(158.75, -56.5) * mm});
            skArc(sketch, "E205.filletArc", {"start": v(155.87, -50.83) * mm, "mid": v(159.56, -54) * mm, "end": v(164.4, -53.6) * mm});
            skArc(sketch, "E206.MirrorCS", {"start": v(129.35, 1.22) * mm, "mid": v(128.96, 6.06) * mm, "end": v(132.12, 9.76) * mm});
            skLineSegment(sketch, "E207.MirrorCS", {"start": v(145.7, 16.68) * mm, "end": v(133.02, 41.57) * mm});
            skLineSegment(sketch, "E208.MirrorCS", {"start": v(132.12, 9.76) * mm, "end": v(145.7, 16.68) * mm});
            skPoint(sketch, "E209.MirrorP", {"position": v(126.46, 6.88) * mm});
            skLineSegment(sketch, "E210.MirrorCS", {"start": v(172.42, -24.58) * mm, "end": v(192.8, -14.2) * mm});
            skLineSegment(sketch, "E211.MirrorCS", {"start": v(142.6, -24.8) * mm, "end": v(129.35, 1.22) * mm});
            skLineSegment(sketch, "E212.MirrorCS", {"start": v(192.8, -14.2) * mm, "end": v(186.74, -2.32) * mm});
            skLineSegment(sketch, "E213", {"start": v(172.42, -24.58) * mm, "end": v(195.2, -69.28) * mm});
            skPoint(sketch, "E214.visualSharp", {"position": v(-222.25, 156.21) * mm});
            skArc(sketch, "E214.filletArc", {"start": v(-203.2, 156.21) * mm, "mid": v(-216.67, 150.63) * mm, "end": v(-222.25, 137.16) * mm});
            skPoint(sketch, "E215.visualSharp", {"position": v(222.25, 156.21) * mm});
            skArc(sketch, "E215.filletArc", {"start": v(222.25, 137.16) * mm, "mid": v(216.67, 150.63) * mm, "end": v(203.2, 156.21) * mm});
            skPoint(sketch, "E216.visualSharp", {"position": v(222.25, -156.2) * mm});
            skArc(sketch, "E216.filletArc", {"start": v(203.2, -156.2) * mm, "mid": v(216.67, -150.63) * mm, "end": v(222.25, -137.16) * mm});
            skPoint(sketch, "E217.visualSharp", {"position": v(-222.25, -156.2) * mm});
            skArc(sketch, "E217.filletArc", {"start": v(-222.25, -137.16) * mm, "mid": v(-216.67, -150.63) * mm, "end": v(-203.2, -156.21) * mm});
            skPoint(sketch, "E218.visualSharp", {"position": v(-196.85, -27.94) * mm});
            skArc(sketch, "E218.filletArc", {"start": v(-196.85, -21.59) * mm, "mid": v(-195, -26.08) * mm, "end": v(-190.5, -27.94) * mm, "construction": true});
            skPoint(sketch, "E219.visualSharp", {"position": v(31.75, -27.94) * mm});
            skArc(sketch, "E219.filletArc", {"start": v(25.4, -27.94) * mm, "mid": v(29.9, -26.08) * mm, "end": v(31.75, -21.59) * mm, "construction": true});
            skPoint(sketch, "E220.visualSharp", {"position": v(-196.85, 137.16) * mm});
            skArc(sketch, "E220.filletArc", {"start": v(-190.5, 137.16) * mm, "mid": v(-195, 135.3) * mm, "end": v(-196.85, 130.81) * mm, "construction": true});
            skPoint(sketch, "E221.visualSharp", {"position": v(31.75, 137.16) * mm});
            skArc(sketch, "E221.filletArc", {"start": v(31.75, 130.81) * mm, "mid": v(29.9, 135.3) * mm, "end": v(25.4, 137.16) * mm, "construction": true});
            skLineSegment(sketch, "E222.bottom", {"start": v(63.5, 88.9) * mm, "end": v(63.5, 124.46) * mm});
            skLineSegment(sketch, "E222.top", {"start": v(196.85, 88.9) * mm, "end": v(196.85, 112.08) * mm});
            skLineSegment(sketch, "E222.left", {"start": v(69.85, 82.55) * mm, "end": v(146.05, 82.55) * mm});
            skLineSegment(sketch, "E222.right", {"start": v(69.85, 130.81) * mm, "end": v(190.5, 130.81) * mm});
            skLineSegment(sketch, "E223.bottom", {"start": v(147.32, 81.28) * mm, "end": v(147.32, 63.5) * mm});
            skLineSegment(sketch, "E223.top", {"start": v(166.37, 81.28) * mm, "end": v(166.37, 63.5) * mm});
            skLineSegment(sketch, "E223.right", {"start": v(153.67, 57.15) * mm, "end": v(160.02, 57.15) * mm});
            skLineSegment(sketch, "E224.trimOffspring", {"start": v(167.64, 82.55) * mm, "end": v(190.5, 82.55) * mm});
            skLineSegment(sketch, "E225", {"start": v(147.32, 82.55) * mm, "end": v(166.37, 82.55) * mm, "construction": true});
            skPoint(sketch, "E226.visualSharp", {"position": v(63.5, 82.55) * mm});
            skArc(sketch, "E226.filletArc", {"start": v(63.5, 88.9) * mm, "mid": v(65.36, 84.4) * mm, "end": v(69.85, 82.55) * mm});
            skPoint(sketch, "E227.visualSharp", {"position": v(196.85, 82.55) * mm});
            skArc(sketch, "E227.filletArc", {"start": v(190.5, 82.55) * mm, "mid": v(195, 84.4) * mm, "end": v(196.85, 88.9) * mm});
            skPoint(sketch, "E228.visualSharp", {"position": v(196.85, 130.81) * mm});
            skArc(sketch, "E228.filletArc", {"start": v(196.85, 124.46) * mm, "mid": v(195, 128.95) * mm, "end": v(190.5, 130.81) * mm});
            skPoint(sketch, "E229.visualSharp", {"position": v(63.5, 130.81) * mm});
            skArc(sketch, "E229.filletArc", {"start": v(69.85, 130.81) * mm, "mid": v(65.36, 128.95) * mm, "end": v(63.5, 124.46) * mm});
            skPoint(sketch, "E230.visualSharp", {"position": v(147.32, 57.15) * mm});
            skArc(sketch, "E230.filletArc", {"start": v(147.32, 63.5) * mm, "mid": v(149.18, 59) * mm, "end": v(153.67, 57.15) * mm});
            skPoint(sketch, "E231.visualSharp", {"position": v(166.37, 57.15) * mm});
            skArc(sketch, "E231.filletArc", {"start": v(160.02, 57.15) * mm, "mid": v(164.51, 59) * mm, "end": v(166.37, 63.5) * mm});
            skLineSegment(sketch, "E232.bottom", {"start": v(173.74, -91.44) * mm, "end": v(196.85, -91.44) * mm, "construction": true});
            skLineSegment(sketch, "E232.left", {"start": v(173.74, -91.44) * mm, "end": v(173.74, -116.84) * mm});
            skLineSegment(sketch, "E232.right", {"start": v(196.85, -91.44) * mm, "end": v(196.85, -116.84) * mm});
            skArc(sketch, "E233", {"start": v(173.74, -116.84) * mm, "mid": v(185.3, -128.4) * mm, "end": v(196.85, -116.84) * mm});
            skLineSegment(sketch, "E234.bottom", {"start": v(-196.85, -139.7) * mm, "end": v(-196.85, -44.45) * mm, "construction": true});
            skLineSegment(sketch, "E234.top", {"start": v(31.75, -139.7) * mm, "end": v(31.75, -44.45) * mm, "construction": true});
            skLineSegment(sketch, "E234.left", {"start": v(-196.85, -139.7) * mm, "end": v(31.75, -139.7) * mm, "construction": true});
            skLineSegment(sketch, "E234.right", {"start": v(-196.85, -44.45) * mm, "end": v(31.75, -44.45) * mm, "construction": true});
            skLineSegment(sketch, "E235", {"start": v(-196.85, -92.07) * mm, "end": v(31.75, -92.07) * mm, "construction": true});
            skLineSegment(sketch, "E236", {"start": v(-196.85, -123.82) * mm, "end": v(31.75, -123.82) * mm, "construction": true});
            skLineSegment(sketch, "E237.MirrorCS", {"start": v(-196.85, -60.32) * mm, "end": v(31.75, -60.32) * mm, "construction": true});
            skLineSegment(sketch, "E238", {"start": v(-196.85, -127.63) * mm, "end": v(31.75, -127.63) * mm, "construction": true});
            skLineSegment(sketch, "E239.MirrorCS", {"start": v(-196.85, -56.51) * mm, "end": v(31.75, -56.51) * mm, "construction": true});
            skLineSegment(sketch, "E240", {"start": v(-177.16, -139.7) * mm, "end": v(-177.16, -44.45) * mm, "construction": true});
            skLineSegment(sketch, "E241", {"start": v(-133.35, -139.7) * mm, "end": v(-133.35, -44.45) * mm, "construction": true});
            skLineSegment(sketch, "E242", {"start": v(-12.7, -139.7) * mm, "end": v(-12.7, -44.45) * mm, "construction": true});
            skLineSegment(sketch, "E243", {"start": v(-196.85, -120.79) * mm, "end": v(-196.85, -63.36) * mm});
            skLineSegment(sketch, "E244", {"start": v(-194.49, -58.42) * mm, "end": v(-178.9, -45.86) * mm});
            skLineSegment(sketch, "E245", {"start": v(-174.92, -44.45) * mm, "end": v(-133.35, -44.45) * mm});
            skLineSegment(sketch, "E246", {"start": v(-133.35, -44.45) * mm, "end": v(-12.7, -56.51) * mm});
            skLineSegment(sketch, "E247", {"start": v(-12.7, -56.51) * mm, "end": v(25.4, -56.51) * mm});
            skLineSegment(sketch, "E248", {"start": v(31.75, -62.86) * mm, "end": v(31.75, -121.28) * mm});
            skLineSegment(sketch, "E249", {"start": v(25.4, -127.63) * mm, "end": v(-12.7, -127.63) * mm});
            skLineSegment(sketch, "E250", {"start": v(-12.7, -127.63) * mm, "end": v(-133.35, -139.7) * mm});
            skLineSegment(sketch, "E251", {"start": v(-133.35, -139.7) * mm, "end": v(-174.92, -139.7) * mm});
            skLineSegment(sketch, "E252", {"start": v(-178.9, -138.3) * mm, "end": v(-194.49, -125.73) * mm});
            skPoint(sketch, "E253.visualSharp", {"position": v(31.75, -127.63) * mm});
            skArc(sketch, "E253.filletArc", {"start": v(25.4, -127.63) * mm, "mid": v(29.9, -125.78) * mm, "end": v(31.75, -121.28) * mm});
            skPoint(sketch, "E254.visualSharp", {"position": v(31.75, -56.51) * mm});
            skArc(sketch, "E254.filletArc", {"start": v(31.75, -62.86) * mm, "mid": v(29.9, -58.37) * mm, "end": v(25.4, -56.51) * mm});
            skPoint(sketch, "E255.visualSharp", {"position": v(-196.85, -123.82) * mm});
            skArc(sketch, "E255.filletArc", {"start": v(-196.85, -120.79) * mm, "mid": v(-196.23, -123.53) * mm, "end": v(-194.49, -125.73) * mm});
            skPoint(sketch, "E256.visualSharp", {"position": v(-177.16, -139.7) * mm});
            skArc(sketch, "E256.filletArc", {"start": v(-178.9, -138.3) * mm, "mid": v(-177.04, -139.34) * mm, "end": v(-174.92, -139.7) * mm});
            skPoint(sketch, "E257.visualSharp", {"position": v(-196.85, -60.32) * mm});
            skArc(sketch, "E257.filletArc", {"start": v(-194.49, -58.42) * mm, "mid": v(-196.23, -60.62) * mm, "end": v(-196.85, -63.36) * mm});
            skPoint(sketch, "E258.visualSharp", {"position": v(-177.16, -44.45) * mm});
            skArc(sketch, "E258.filletArc", {"start": v(-174.92, -44.45) * mm, "mid": v(-177.04, -44.81) * mm, "end": v(-178.9, -45.86) * mm});
            skLineSegment(sketch, "E259", {"start": v(173.74, -116.84) * mm, "end": v(196.85, -116.84) * mm, "construction": true});
            skLineSegment(sketch, "E260.MirrorCS", {"start": v(160.32, -0.82) * mm, "end": v(137.54, 43.88) * mm});
            skLineSegment(sketch, "E261.MirrorCS", {"start": v(133.02, 41.57) * mm, "end": v(137.54, 43.88) * mm});
            skLineSegment(sketch, "E262", {"start": v(198.12, 122.87) * mm, "end": v(198.76, 122.87) * mm});
            skLineSegment(sketch, "E263", {"start": v(200.03, 121.6) * mm, "end": v(200.03, 114.62) * mm});
            skLineSegment(sketch, "E264", {"start": v(198.76, 113.35) * mm, "end": v(198.12, 113.35) * mm});
            skPoint(sketch, "E265.visualSharp", {"position": v(166.37, 82.55) * mm});
            skArc(sketch, "E265.filletArc", {"start": v(167.64, 82.55) * mm, "mid": v(166.74, 82.18) * mm, "end": v(166.37, 81.28) * mm});
            skPoint(sketch, "E266.visualSharp", {"position": v(147.32, 82.55) * mm});
            skArc(sketch, "E266.filletArc", {"start": v(147.32, 81.28) * mm, "mid": v(146.95, 82.18) * mm, "end": v(146.05, 82.55) * mm});
            skPoint(sketch, "E267.visualSharp", {"position": v(200.03, 113.35) * mm});
            skArc(sketch, "E267.filletArc", {"start": v(198.76, 113.35) * mm, "mid": v(199.65, 113.72) * mm, "end": v(200.03, 114.62) * mm});
            skPoint(sketch, "E268.visualSharp", {"position": v(200.03, 122.87) * mm});
            skArc(sketch, "E268.filletArc", {"start": v(200.03, 121.6) * mm, "mid": v(199.65, 122.5) * mm, "end": v(198.76, 122.87) * mm});
            skPoint(sketch, "E269.visualSharp", {"position": v(196.85, 122.87) * mm});
            skArc(sketch, "E269.filletArc", {"start": v(196.85, 124.13) * mm, "mid": v(197.23, 123.24) * mm, "end": v(198.12, 122.87) * mm});
            skPoint(sketch, "E270.visualSharp", {"position": v(196.85, 113.35) * mm});
            skArc(sketch, "E270.filletArc", {"start": v(198.12, 113.35) * mm, "mid": v(197.22, 112.98) * mm, "end": v(196.85, 112.08) * mm});
            skLineSegment(sketch, "E271", {"start": v(-196.85, 54.61) * mm, "end": v(31.75, 54.61) * mm, "construction": true});
            skLineSegment(sketch, "E272", {"start": v(-82.55, -27.94) * mm, "end": v(-82.55, 137.16) * mm, "construction": true});
            skLineSegment(sketch, "E273", {"start": v(0, 156.21) * mm, "end": v(0, -156.2) * mm, "construction": true});
            skLineSegment(sketch, "E274", {"start": v(-222.25, 0) * mm, "end": v(222.25, 0) * mm, "construction": true});
            skPoint(sketch, "E275", {"position": v(0, 0) * mm});
            skPoint(sketch, "E276", {"position": v(-82.55, 54.61) * mm});
            skPoint(sketch, "E277", {"position": v(-133.35, -92.07) * mm});
            skLineSegment(sketch, "E278", {"start": v(63.5, 106.68) * mm, "end": v(196.85, 106.68) * mm, "construction": true});
            skLineSegment(sketch, "E279", {"start": v(130.18, 130.81) * mm, "end": v(130.18, 82.55) * mm, "construction": true});
            skPoint(sketch, "E280", {"position": v(130.18, 106.68) * mm});
            skLineSegment(sketch, "E281", {"start": v(172.42, -24.58) * mm, "end": v(160.32, -0.82) * mm, "construction": true});
            skPoint(sketch, "E282", {"position": v(166.37, -12.7) * mm});
            skLineSegment(sketch, "E283", {"start": v(196.85, 124.46) * mm, "end": v(196.85, 124.13) * mm});
            skLineSegment(sketch, "E284", {"start": v(196.85, 124.13) * mm, "end": v(196.85, 112.08) * mm, "construction": true});
            skArc(sketch, "E285", {"start": v(31.75, -21.59) * mm, "mid": v(29.9, -26.08) * mm, "end": v(25.4, -27.94) * mm, "construction": true});
            skLineSegment(sketch, "E286.bottom", {"start": v(107.95, -137.16) * mm, "end": v(57.15, -137.16) * mm});
            skLineSegment(sketch, "E286.top", {"start": v(107.95, 66.04) * mm, "end": v(57.15, 66.04) * mm});
            skLineSegment(sketch, "E286.left", {"start": v(114.3, -130.8) * mm, "end": v(114.3, 59.69) * mm});
            skLineSegment(sketch, "E286.right", {"start": v(50.8, -130.8) * mm, "end": v(50.8, 59.69) * mm});
            skLineSegment(sketch, "E287", {"start": v(82.55, -137.16) * mm, "end": v(82.55, 66.04) * mm, "construction": true});
            skLineSegment(sketch, "E288", {"start": v(114.3, -35.56) * mm, "end": v(50.8, -35.56) * mm, "construction": true});
            skPoint(sketch, "E289", {"position": v(82.55, -35.56) * mm});
            skPoint(sketch, "E290.visualSharp", {"position": v(114.3, -137.16) * mm});
            skArc(sketch, "E290.filletArc", {"start": v(107.95, -137.16) * mm, "mid": v(112.44, -135.3) * mm, "end": v(114.3, -130.8) * mm});
            skPoint(sketch, "E291.visualSharp", {"position": v(50.8, -137.16) * mm});
            skArc(sketch, "E291.filletArc", {"start": v(50.8, -130.8) * mm, "mid": v(52.66, -135.3) * mm, "end": v(57.15, -137.16) * mm});
            skPoint(sketch, "E292.visualSharp", {"position": v(50.8, 66.04) * mm});
            skArc(sketch, "E292.filletArc", {"start": v(57.15, 66.04) * mm, "mid": v(52.66, 64.18) * mm, "end": v(50.8, 59.69) * mm});
            skPoint(sketch, "E293.visualSharp", {"position": v(114.3, 66.04) * mm});
            skArc(sketch, "E293.filletArc", {"start": v(114.3, 59.69) * mm, "mid": v(112.44, 64.18) * mm, "end": v(107.95, 66.04) * mm});
            skLineSegment(sketch, "E294", {"start": v(185.3, -91.44) * mm, "end": v(185.3, -128.4) * mm, "construction": true});
            skLineSegment(sketch, "E295.bottom", {"start": v(-193.68, 143.5) * mm, "end": v(-193.68, 143.5) * mm});
            skLineSegment(sketch, "E295.top", {"start": v(-193.68, -34.3) * mm, "end": v(3.17, -34.3) * mm});
            skLineSegment(sketch, "E295.left", {"start": v(-206.38, 130.8) * mm, "end": v(-206.38, 130.8) * mm});
            skLineSegment(sketch, "E295.right", {"start": v(41.28, 130.8) * mm, "end": v(41.28, 121.33) * mm, "construction": true});
            skPoint(sketch, "E296.visualSharp", {"position": v(-206.38, 143.5) * mm});
            skArc(sketch, "E296.filletArc", {"start": v(-193.68, 143.5) * mm, "mid": v(-202.66, 139.8) * mm, "end": v(-206.38, 130.8) * mm});
            skPoint(sketch, "E297.visualSharp", {"position": v(41.28, 143.5) * mm});
            skArc(sketch, "E297.filletArc", {"start": v(41.28, 130.8) * mm, "mid": v(37.56, 139.8) * mm, "end": v(28.58, 143.51) * mm});
            skPoint(sketch, "E298.visualSharp", {"position": v(41.27, -34.3) * mm});
            skArc(sketch, "E298.filletArc", {"start": v(28.57, -34.3) * mm, "mid": v(37.56, -30.57) * mm, "end": v(41.27, -21.6) * mm});
            skPoint(sketch, "E299.visualSharp", {"position": v(-206.38, -34.3) * mm});
            skArc(sketch, "E299.filletArc", {"start": v(-206.38, -21.6) * mm, "mid": v(-202.66, -30.57) * mm, "end": v(-193.68, -34.3) * mm});
            skArc(sketch, "E300", {"start": v(-206.38, 62.23) * mm, "mid": v(-214, 54.6) * mm, "end": v(-206.38, 46.99) * mm});
            skLineSegment(sketch, "E301", {"start": v(-206.38, 62.23) * mm, "end": v(-206.38, 46.99) * mm, "construction": true});
            skLineSegment(sketch, "E302", {"start": v(-206.38, 46.99) * mm, "end": v(-206.38, -21.6) * mm});
            skArc(sketch, "E303", {"start": v(124.46, -93.98) * mm, "mid": v(139.7, -78.74) * mm, "end": v(154.94, -93.98) * mm});
            skArc(sketch, "E304", {"start": v(154.94, -124.46) * mm, "mid": v(139.7, -139.7) * mm, "end": v(124.46, -124.46) * mm});
            skArc(sketch, "E305", {"start": v(173.74, -91.44) * mm, "mid": v(185.3, -79.88) * mm, "end": v(196.85, -91.44) * mm});
            skLineSegment(sketch, "E306", {"start": v(-193.68, 121.28) * mm, "end": v(3.18, 121.28) * mm});
            skLineSegment(sketch, "E307", {"start": v(15.88, 108.58) * mm, "end": v(15.87, -21.6) * mm});
            skPoint(sketch, "E308.visualSharp", {"position": v(15.88, 121.28) * mm});
            skArc(sketch, "E308.filletArc", {"start": v(15.88, 108.58) * mm, "mid": v(12.16, 117.57) * mm, "end": v(3.18, 121.28) * mm});
            skLineSegment(sketch, "E309", {"start": v(-206.38, 108.58) * mm, "end": v(-206.38, 62.23) * mm});
            skLineSegment(sketch, "E310", {"start": v(15.87, -34.3) * mm, "end": v(19, -34.3) * mm});
            skPoint(sketch, "E311.visualSharp", {"position": v(-206.38, 121.28) * mm});
            skArc(sketch, "E311.filletArc", {"start": v(-193.68, 121.28) * mm, "mid": v(-202.66, 117.57) * mm, "end": v(-206.38, 108.58) * mm});
            skPoint(sketch, "E312.visualSharp", {"position": v(15.87, -34.3) * mm});
            skArc(sketch, "E312.filletArc", {"start": v(3.17, -34.3) * mm, "mid": v(12.16, -30.57) * mm, "end": v(15.87, -21.6) * mm});
            skLineSegment(sketch, "E313", {"start": v(-206.38, 121.28) * mm, "end": v(-206.38, 110.32) * mm});
            skLineSegment(sketch, "E314", {"start": v(15.87, -34.3) * mm, "end": v(11.1, -34.3) * mm});
            skLineSegment(sketch, "E315", {"start": v(173.74, -106.68) * mm, "end": v(196.85, -106.68) * mm});
            skPoint(sketch, "E316", {"position": v(-206.38, 110.3) * mm});
            skPoint(sketch, "E317", {"position": v(-184.15, 143.5) * mm});
            skPoint(sketch, "E318", {"position": v(-158.75, 143.5) * mm});
            skPoint(sketch, "E319", {"position": v(-149.23, 143.5) * mm});
            skPoint(sketch, "E320", {"position": v(-123.83, 143.5) * mm});
            skPoint(sketch, "E321", {"position": v(-114.3, 143.5) * mm});
            skPoint(sketch, "E322", {"position": v(-88.9, 143.5) * mm});
            skPoint(sketch, "E323", {"position": v(-79.38, 143.5) * mm});
            skPoint(sketch, "E324", {"position": v(-53.97, 143.5) * mm});
            skPoint(sketch, "E325", {"position": v(-44.45, 143.5) * mm});
            skPoint(sketch, "E326", {"position": v(-19.05, 143.5) * mm});
            skPoint(sketch, "E327", {"position": v(-9.52, 143.5) * mm});
            skPoint(sketch, "E328", {"position": v(19.05, 143.5) * mm});
            skPoint(sketch, "E329", {"position": v(41.28, 121.28) * mm});
            skPoint(sketch, "E330", {"position": v(41.28, 95.88) * mm});
            skPoint(sketch, "E331", {"position": v(41.28, 86.36) * mm});
            skPoint(sketch, "E332", {"position": v(41.27, 60.96) * mm});
            skPoint(sketch, "E333", {"position": v(41.28, 51.43) * mm});
            skPoint(sketch, "E334", {"position": v(41.28, 54.6) * mm});
            skPoint(sketch, "E335", {"position": v(41.27, 26.03) * mm});
            skPoint(sketch, "E336", {"position": v(41.27, 16.5) * mm});
            skPoint(sketch, "E337", {"position": v(41.27, -12.07) * mm});
            skPoint(sketch, "E338", {"position": v(19.05, -34.3) * mm});
            skPoint(sketch, "E339", {"position": v(11.23, -34.3) * mm});
            skPoint(sketch, "E340", {"position": v(-206.38, 103.96) * mm});
            skPoint(sketch, "E341", {"position": v(4.88, -34.3) * mm});
            skLineSegment(sketch, "E342", {"start": v(-206.38, 110.32) * mm, "end": v(-206.38, 103.95) * mm, "construction": true});
            skLineSegment(sketch, "E343", {"start": v(-206.38, 108.58) * mm, "end": v(-206.38, 103.95) * mm});
            skLineSegment(sketch, "E344", {"start": v(-206.38, 130.8) * mm, "end": v(-206.38, 126.05) * mm, "construction": true});
            skLineSegment(sketch, "E345", {"start": v(-193.68, 143.5) * mm, "end": v(-184.33, 143.5) * mm, "construction": true});
            skLineSegment(sketch, "E346", {"start": v(-184.33, 143.5) * mm, "end": v(-158.7, 143.5) * mm});
            skLineSegment(sketch, "E347", {"start": v(-149.24, 143.5) * mm, "end": v(-123.98, 143.5) * mm});
            skLineSegment(sketch, "E348", {"start": v(-123.98, 143.5) * mm, "end": v(-114.26, 143.5) * mm, "construction": true});
            skLineSegment(sketch, "E349", {"start": v(-88.83, 143.5) * mm, "end": v(-79.25, 143.5) * mm, "construction": true});
            skLineSegment(sketch, "E350", {"start": v(-53.9, 143.5) * mm, "end": v(-44.37, 143.5) * mm, "construction": true});
            skLineSegment(sketch, "E351", {"start": v(-18.87, 143.5) * mm, "end": v(-9.66, 143.5) * mm, "construction": true});
            skLineSegment(sketch, "E352", {"start": v(-9.66, 143.5) * mm, "end": v(19.21, 143.5) * mm});
            skLineSegment(sketch, "E353", {"start": v(41.28, 121.33) * mm, "end": v(41.28, 96.14) * mm});
            skLineSegment(sketch, "E354", {"start": v(41.28, 96.14) * mm, "end": v(41.28, 86.93) * mm, "construction": true});
            skLineSegment(sketch, "E355", {"start": v(41.28, 86.93) * mm, "end": v(41.28, 61.3) * mm});
            skLineSegment(sketch, "E356", {"start": v(41.28, 61.3) * mm, "end": v(41.28, 51.84) * mm, "construction": true});
            skLineSegment(sketch, "E357", {"start": v(41.28, 51.84) * mm, "end": v(41.27, 26.06) * mm});
            skLineSegment(sketch, "E358", {"start": v(41.27, 26.06) * mm, "end": v(41.27, 16.63) * mm, "construction": true});
            skLineSegment(sketch, "E359", {"start": v(41.27, 16.63) * mm, "end": v(41.27, -11.65) * mm});
            skLineSegment(sketch, "E360", {"start": v(41.27, -11.65) * mm, "end": v(41.27, -21.6) * mm, "construction": true});
            skLineSegment(sketch, "E361", {"start": v(19, -34.3) * mm, "end": v(28.57, -34.3) * mm, "construction": true});
            skLineSegment(sketch, "E362", {"start": v(4.85, -34.3) * mm, "end": v(3.17, -34.3) * mm});
            skLineSegment(sketch, "E363", {"start": v(11.1, -34.3) * mm, "end": v(4.85, -34.3) * mm, "construction": true});
            skLineSegment(sketch, "E364", {"start": v(-158.7, 143.5) * mm, "end": v(-149.24, 143.5) * mm, "construction": true});
            skLineSegment(sketch, "E365", {"start": v(-114.26, 143.5) * mm, "end": v(-88.83, 143.5) * mm});
            skLineSegment(sketch, "E366", {"start": v(-79.25, 143.5) * mm, "end": v(-53.9, 143.5) * mm});
            skLineSegment(sketch, "E367", {"start": v(-44.37, 143.5) * mm, "end": v(-18.87, 143.5) * mm});
            skLineSegment(sketch, "E368", {"start": v(19.21, 143.5) * mm, "end": v(28.58, 143.5) * mm, "construction": true});
            skLineSegment(sketch, "E369", {"start": v(-206.38, 126.05) * mm, "end": v(-206.38, 121.28) * mm});
            skSolve(sketch);
        }
        {
            var Q0;
            Q0=qSketchRegion(id+"F4",true);
            extrude(context, id + "F5", {"entities" : qUnion([Q0]), "depth" : 12.7 * mm, "offsetDistance" : 25.4 * mm});
        }
    });
